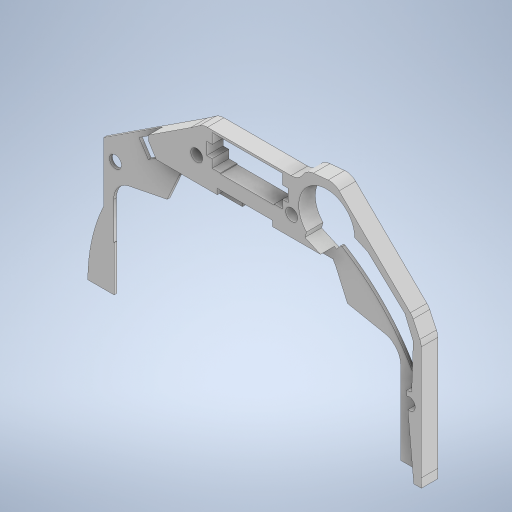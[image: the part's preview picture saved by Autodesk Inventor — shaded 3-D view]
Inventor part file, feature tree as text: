
AUTODESK INVENTOR PART (.ipt)
format: ipt  version: 2023.4 (Build 274418000, 418)  size: 444,928 bytes
history: native  units: mm
features: extrude x2, sketch x2, projected_geometry x1
ambient origin geometry x8: Origin, YZ Plane, XZ Plane, XY Plane, X Axis, Y Axis, Z Axis, Center Point
bodies: Solid1 (feature_tree)
feature tree (5):
  extrude  "Extrusion1"  Depth=5.0mm TaperAngle=0.0deg
  extrude  "Extrusion2"  Depth=0.872665mm
  sketch  "Sketch1"  dims[d0=1.0mm d1=0.0mm d2=5.0mm d3=0.0mm]
  sketch  "Sketch2"  dims[d4=0.5mm d5=0.872665mm]
  projected_geometry  "Projected Loop1"
